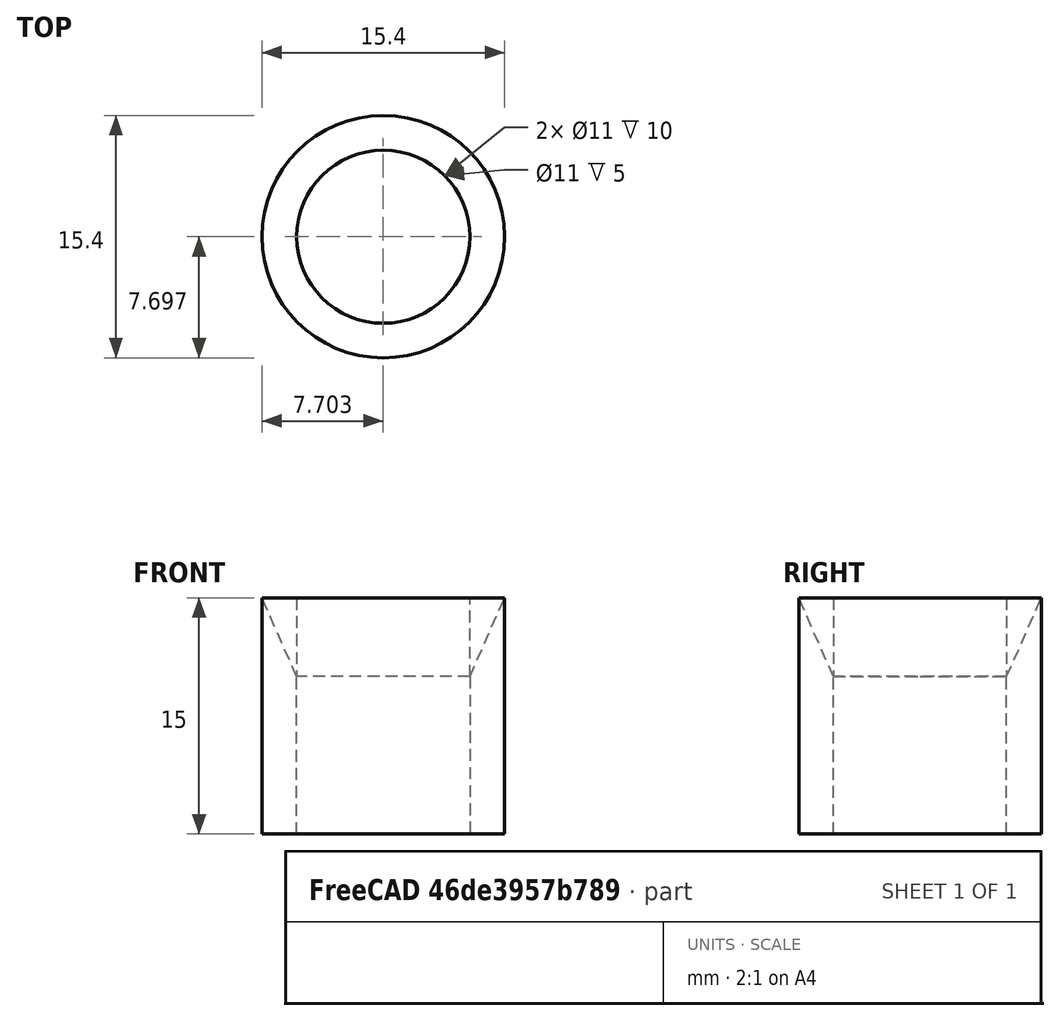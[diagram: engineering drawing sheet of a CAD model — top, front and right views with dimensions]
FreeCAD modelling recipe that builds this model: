
FCSTD DOCUMENT  (FreeCAD 0.18.4R)
Label: spillway.extender
License: All rights reserved
LicenseURL: http://en.wikipedia.org/wiki/All_rights_reserved
objects: Part::Extrusion×3, Part::Feature×3, Part::Part2DObjectPython×2, Part::Cut×2, Part::MultiFuse×1
note: 11 computed .brp shape members not serialized (recipe doc carries the construction recipe); baked Part::Feature solids carry a one-line shape summary decoded from their .brp

FEATURE [Part::Part2DObjectPython] Circle  # Draft 2D object (typed FeaturePython)
  FirstAngle = 0
  LastAngle = 0
  MakeFace = true
  Placement = pos=(-1.42729,0.617252,0) rot=(0,0,1;0rad)
  Radius = 7.7
FEATURE [Part::Extrusion] Extrusion
  Base = -> Circle
  Dir = (0,0,10)
  DirMode = 0
  FaceMakerClass = Part::FaceMakerBullseye
  LengthFwd = 0
  LengthRev = 0
  Solid = true
  Symmetric = false
FEATURE [Part::Part2DObjectPython] Circle001  # Draft 2D object (typed FeaturePython)
  FirstAngle = 0
  LastAngle = 0
  MakeFace = true
  Placement = pos=(-1.42729,0.617252,10) rot=(0,0,1;0rad)
  Radius = 5.5
  Support = -> [Extrusion]
FEATURE [Part::Extrusion] Extrusion001
  Base = -> Circle001
  Dir = (0,0,-42.4565)
  DirMode = 0
  FaceMakerClass = Part::FaceMakerBullseye
  LengthFwd = 0
  LengthRev = 0
  Solid = true
  Symmetric = false
FEATURE [Part::Cut] Cut
  Base = -> Extrusion
  Tool = -> Extrusion001
FEATURE [Part::Feature] Face
  shape: bbox 15.4 x 15.4 x 2e-07 mm, 1 faces, 0 solids (baked)
FEATURE [Part::Extrusion] Extrusion002
  Base = -> Face
  Dir = (0,0,5)
  DirMode = 0
  FaceMakerClass = Part::FaceMakerBullseye
  LengthFwd = 0
  LengthRev = 0
  Solid = true
  Symmetric = false
FEATURE [Part::MultiFuse] Fusion
  Shapes = -> [Cut,Extrusion002]
FEATURE [Part::Feature] Fusion001
  shape: bbox 15.4 x 15.4 x 15 mm, 4 faces (baked)
FEATURE [Part::Feature] Cone001
  Placement = pos=(-1.42729,0.617252,10) rot=(0,0,1;0rad)
  shape: bbox 15.4 x 15.4 x 5 mm, 3 faces (baked)
FEATURE [Part::Cut] Cut001
  Base = -> Fusion001
  Tool = -> Cone001
